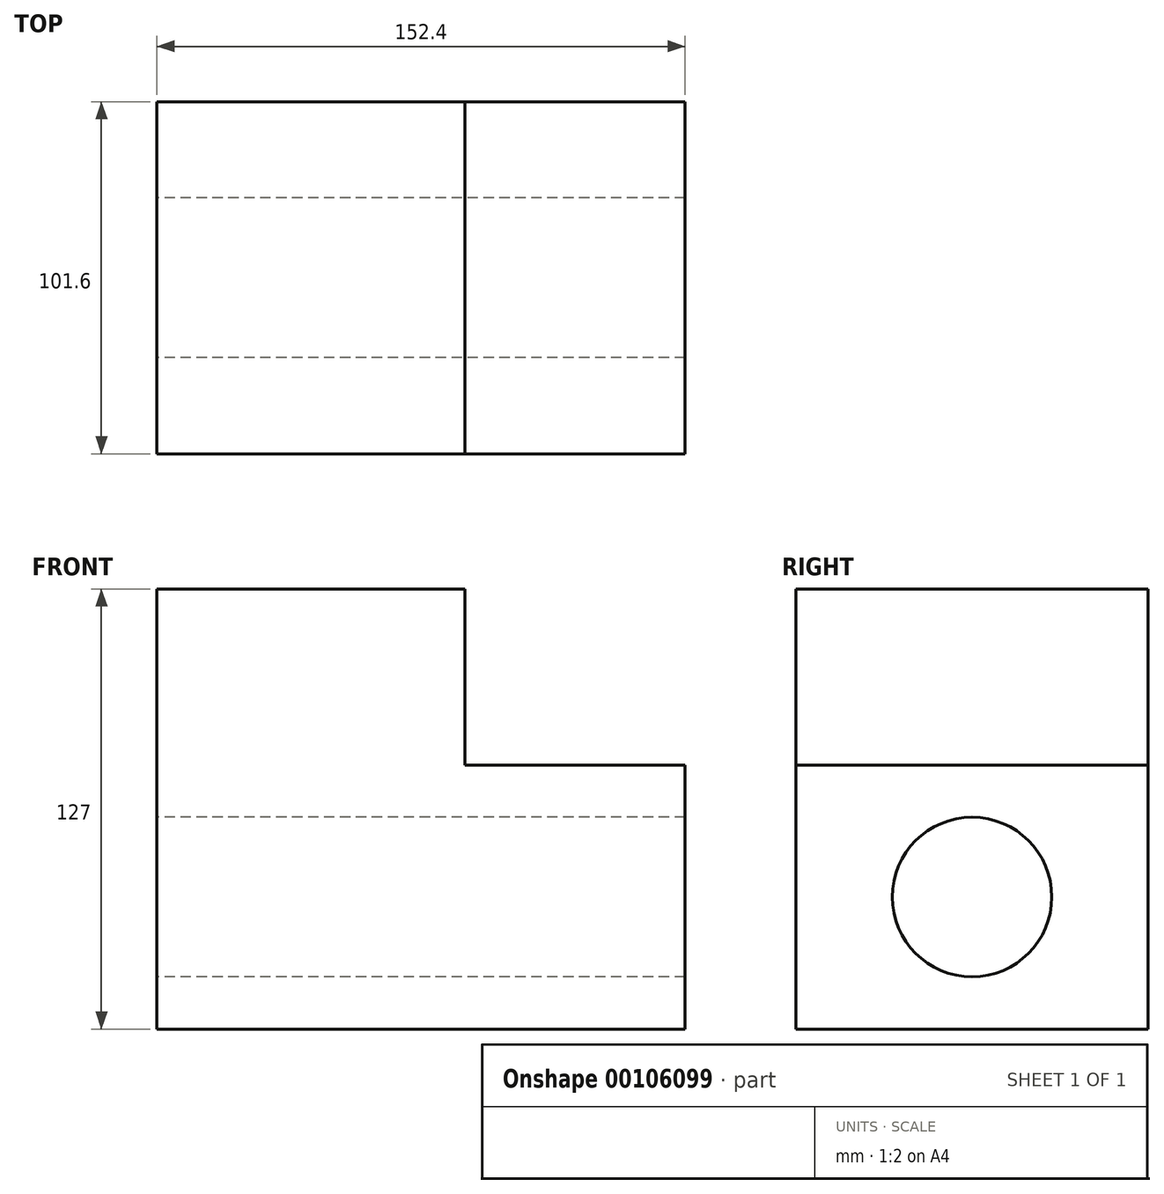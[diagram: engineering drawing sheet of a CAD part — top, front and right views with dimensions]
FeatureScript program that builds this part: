
annotation { "Feature Type Name" : "Feature", "Feature Type Description" : "" }
export const myFeature = defineFeature(function(context is Context, id is Id, definition is map)
    precondition{}
    {
        {
            var Q0;
            Q0=qCreatedBy(makeId("Top.planeOp"),FACE);
            var sketch = newSketch(context, id + "F0", { "sketchPlane" : qUnion([Q0])});
            skLineSegment(sketch, "E0.bottom", {"start": v(-48.76, 60.3) * mm, "end": v(103.64, 60.3) * mm});
            skLineSegment(sketch, "E0.top", {"start": v(-48.76, -41.3) * mm, "end": v(103.64, -41.3) * mm});
            skLineSegment(sketch, "E0.left", {"start": v(-48.76, 60.3) * mm, "end": v(-48.76, -41.3) * mm});
            skLineSegment(sketch, "E0.right", {"start": v(103.64, 60.3) * mm, "end": v(103.64, -41.3) * mm});
            skSolve(sketch);
        }
        {
            var Q0;
            Q0=makeQuery(id+"F0.imprint","IMPRINT",FACE,{"disambiguationData":[TD([[makeQuery(id+"F0.imprint","IMPRINT",EDGE,{"derivedFrom":sQuery(id+"F0.wireOp",EDGE,"E0.bottom")}),-1.0]])]});
            extrude(context, id + "F1", {"entities" : qUnion([Q0]), "depth" : 127 * mm});
        }
        {
            var Q0;
            Q0=makeQuery(id+"F1.opExtrude","SWEPT_FACE",FACE,{"disambiguationData":[OSD([sQuery(id+"F0.wireOp",EDGE,"E0.top")])]});
            var sketch = newSketch(context, id + "F2", { "sketchPlane" : qUnion([Q0])});
            skLineSegment(sketch, "E1.bottom", {"start": v(103.64, 127) * mm, "end": v(40.14, 127) * mm});
            skLineSegment(sketch, "E1.top", {"start": v(103.64, 76.2) * mm, "end": v(40.14, 76.2) * mm});
            skLineSegment(sketch, "E1.left", {"start": v(103.64, 127) * mm, "end": v(103.64, 76.2) * mm});
            skLineSegment(sketch, "E1.right", {"start": v(40.14, 127) * mm, "end": v(40.14, 76.2) * mm});
            skSolve(sketch);
        }
        {
            var Q0;
            Q0=makeQuery(id+"F2.imprint","IMPRINT",FACE,{"disambiguationData":[TD([[makeQuery(id+"F2.imprint","IMPRINT",EDGE,{"derivedFrom":sQuery(id+"F2.wireOp",EDGE,"E1.bottom")}),-1.0]])]});
            extrude(context, id + "F3", {"entities" : qUnion([Q0]), "operationType" : NewBodyOperationType.REMOVE, "oppositeDirection" : true, "depth" : 103.88 * mm});
        }
        {
            var Q0;
            Q0=makeQuery(id+"F1.opExtrude","SWEPT_FACE",FACE,{"disambiguationData":[OSD([sQuery(id+"F0.wireOp",EDGE,"E0.left")])]});
            var sketch = newSketch(context, id + "F4", { "sketchPlane" : qUnion([Q0])});
            skCircle(sketch, "E2", {"center": v(-9.5, 38.1) * mm, "radius": 23.01 * mm});
            skSolve(sketch);
        }
        {
            var Q0;
            Q0=makeQuery(id+"F4.imprint","IMPRINT",FACE,{"disambiguationData":[TD([[makeQuery(id+"F4.imprint","IMPRINT",EDGE,{"derivedFrom":sQuery(id+"F4.wireOp",EDGE,"E2")}),1.0]])]});
            var sketch = newSketch(context, id + "F5", { "sketchPlane" : qUnion([Q0])});
            skSolve(sketch);
        }
        {
            var Q0;
            Q0=qSketchRegion(id+"F5",true);
            var Q1;
            Q1=makeQuery(id+"F4.imprint","IMPRINT",FACE,{"disambiguationData":[TD([[makeQuery(id+"F4.imprint","IMPRINT",EDGE,{"derivedFrom":sQuery(id+"F4.wireOp",EDGE,"E2")}),1.0]])]});
            extrude(context, id + "F6", {"entities" : qUnion([Q0, Q1]), "operationType" : NewBodyOperationType.REMOVE, "endBound" : BoundingType.THROUGH_ALL, "oppositeDirection" : true, "depth" : 25.4 * mm});
        }
    });
